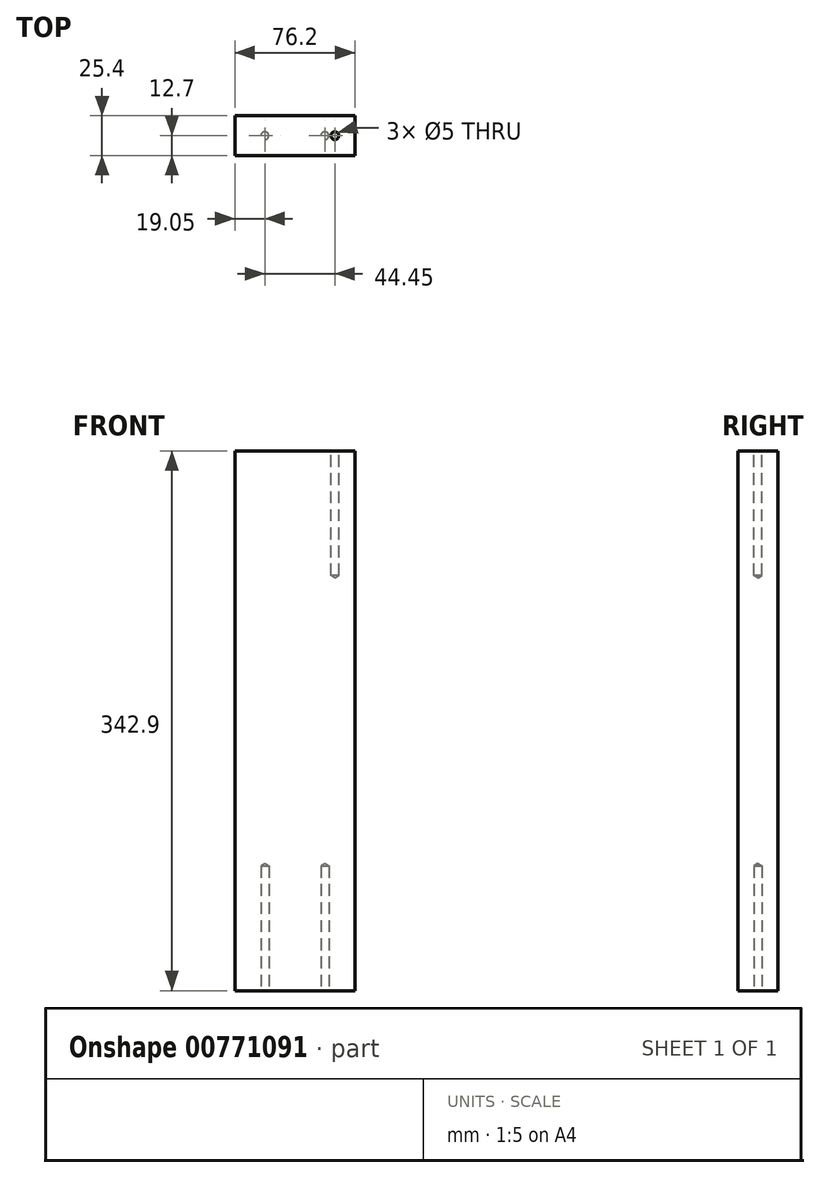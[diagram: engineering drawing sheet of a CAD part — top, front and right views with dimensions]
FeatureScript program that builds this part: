
annotation { "Feature Type Name" : "Feature", "Feature Type Description" : "" }
export const myFeature = defineFeature(function(context is Context, id is Id, definition is map)
    precondition{}
    {
        {
            var Q0;
            Q0=qCreatedBy(makeId("Front.planeOp"),FACE);
            var sketch = newSketch(context, id + "F0", { "sketchPlane" : qUnion([Q0])});
            skLineSegment(sketch, "E0", {"start": v(0, 0) * mm, "end": v(0, 342.9) * mm});
            skLineSegment(sketch, "E1", {"start": v(0, 342.9) * mm, "end": v(76.2, 342.9) * mm});
            skLineSegment(sketch, "E2", {"start": v(0, 0) * mm, "end": v(76.2, 0) * mm});
            skLineSegment(sketch, "E3", {"start": v(76.2, 0) * mm, "end": v(76.2, 342.9) * mm});
            skLineSegment(sketch, "E4", {"start": v(76.2, 342.9) * mm, "end": v(76.2, 342.9) * mm});
            skSolve(sketch);
        }
        {
            var Q0;
            Q0=makeQuery(id+"F0.imprint","IMPRINT",FACE,{"disambiguationData":[TD([[makeQuery(id+"F0.imprint","IMPRINT",EDGE,{"derivedFrom":sQuery(id+"F0.wireOp",EDGE,"E0")}),-1.0]])]});
            extrude(context, id + "F1", {"entities" : qUnion([Q0]), "depth" : 25.4 * mm, "offsetDistance" : 25.4 * mm});
        }
        {
            var Q0;
            Q0=makeQuery(id+"F1.opExtrude","SWEPT_FACE",FACE,{"disambiguationData":[OSD([sQuery(id+"F0.wireOp",EDGE,"E1")])]});
            var sketch = newSketch(context, id + "F2", { "sketchPlane" : qUnion([Q0])});
            skLineSegment(sketch, "E5", {"start": v(76.2, -12.7) * mm, "end": v(63.5, -12.7) * mm});
            skSolve(sketch);
        }
        {
            var Q0;
            Q0=sQuery(id+"F2.wireOp",VERTEX,"E5.end");
            var Q1;
            Q1=makeQuery(id+"F1.opExtrude","SWEPT_BODY",BODY,{"disambiguationData":[OSD([sQuery(id+"F0.wireOp",EDGE,"E0"),sQuery(id+"F0.wireOp",EDGE,"E1"),sQuery(id+"F0.wireOp",EDGE,"E2"),sQuery(id+"F0.wireOp",EDGE,"E3")])]});
            hole(context, id + "F3", {"style" : HoleStyle.SIMPLE, "endStyle" : HoleEndStyle.BLIND, "standardTappedOrClearance" : lookupTablePath({ "standard" : "ISO", "engagement" : "75%", "pitch" : "1 mm", "size" : "M6", "type" : "Tapped" }), "standardBlindInLast" : lookupTablePath({ "standard" : "ISO", "engagement" : "75%", "pitch" : "1 mm", "size" : "M6", "type" : "Tapped" }), "holeDiameter" : 5 * mm, "majorDiameter" : 6 * mm, "showTappedDepth" : true, "holeDepth" : 79.2 * mm, "tappedDepth" : 76.2 * mm, "tapClearance" : 3, "locations" : qUnion([Q0]), "scope" : qUnion([Q1])});
        }
        {
            var Q0;
            Q0=makeQuery(id+"F1.opExtrude","SWEPT_FACE",FACE,{"disambiguationData":[OSD([sQuery(id+"F0.wireOp",EDGE,"E2")])]});
            var sketch = newSketch(context, id + "F4", { "sketchPlane" : qUnion([Q0])});
            skLineSegment(sketch, "E6", {"start": v(76.2, 12.7) * mm, "end": v(57.15, 12.7) * mm});
            skLineSegment(sketch, "E7", {"start": v(0, 12.7) * mm, "end": v(19.05, 12.7) * mm});
            skSolve(sketch);
        }
        {
            var Q0;
            Q0=sQuery(id+"F4.wireOp",VERTEX,"E6.end");
            var Q1;
            Q1=sQuery(id+"F4.wireOp",VERTEX,"E7.end");
            var Q2;
            Q2=makeQuery(id+"F1.opExtrude","SWEPT_BODY",BODY,{"disambiguationData":[OSD([sQuery(id+"F0.wireOp",EDGE,"E0"),sQuery(id+"F0.wireOp",EDGE,"E1"),sQuery(id+"F0.wireOp",EDGE,"E2"),sQuery(id+"F0.wireOp",EDGE,"E3")])]});
            hole(context, id + "F5", {"style" : HoleStyle.SIMPLE, "endStyle" : HoleEndStyle.BLIND, "standardTappedOrClearance" : lookupTablePath({ "standard" : "ISO", "engagement" : "75%", "pitch" : "1 mm", "size" : "M6", "type" : "Tapped" }), "standardBlindInLast" : lookupTablePath({ "standard" : "ISO", "engagement" : "75%", "pitch" : "1 mm", "size" : "M6", "type" : "Tapped" }), "holeDiameter" : 5 * mm, "majorDiameter" : 6 * mm, "showTappedDepth" : true, "holeDepth" : 79.2 * mm, "tappedDepth" : 76.2 * mm, "tapClearance" : 3, "locations" : qUnion([Q0, Q1]), "scope" : qUnion([Q2])});
        }
    });
